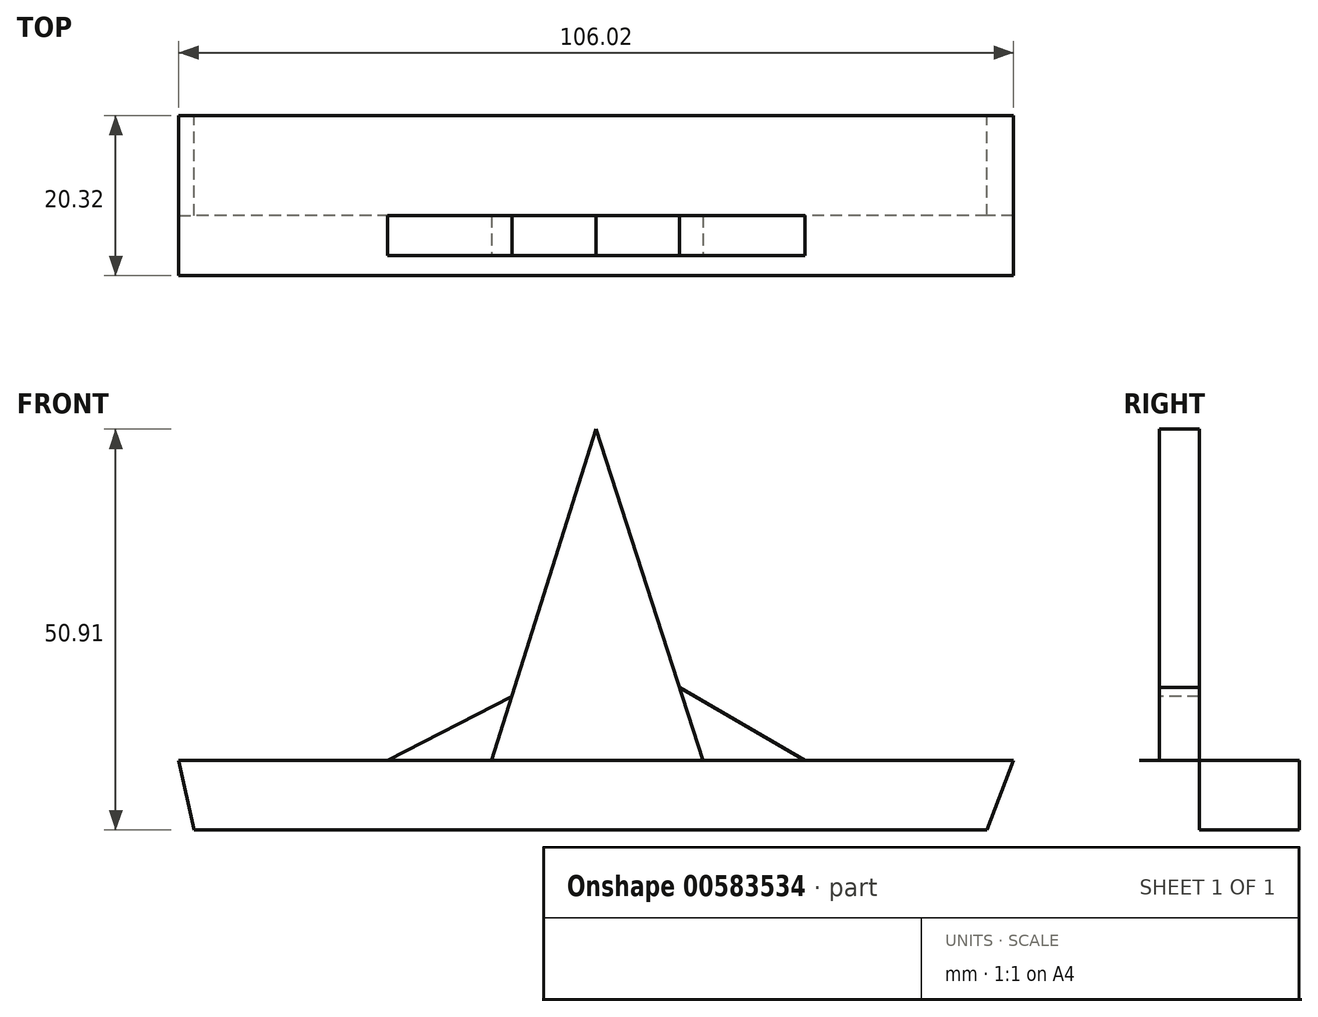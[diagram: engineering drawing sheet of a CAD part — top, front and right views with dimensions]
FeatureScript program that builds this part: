
annotation { "Feature Type Name" : "Feature", "Feature Type Description" : "" }
export const myFeature = defineFeature(function(context is Context, id is Id, definition is map)
    precondition{}
    {
        {
            var Q0;
            Q0=qCreatedBy(makeId("Front.planeOp"),FACE);
            var sketch = newSketch(context, id + "F0", { "sketchPlane" : qUnion([Q0])});
            skLineSegment(sketch, "E0", {"start": v(0, 0) * mm, "end": v(53.01, 0) * mm, "construction": true});
            skLineSegment(sketch, "E1", {"start": v(0, 0) * mm, "end": v(-53.01, 0) * mm, "construction": true});
            skLineSegment(sketch, "E2", {"start": v(-13.29, 0) * mm, "end": v(0, 42.1) * mm});
            skLineSegment(sketch, "E3", {"start": v(0, 42.1) * mm, "end": v(13.57, 0) * mm});
            skLineSegment(sketch, "E4", {"start": v(-53.01, 0) * mm, "end": v(-51.06, -8.81) * mm});
            skLineSegment(sketch, "E5", {"start": v(53.01, 0) * mm, "end": v(49.66, -8.81) * mm});
            skLineSegment(sketch, "E6", {"start": v(49.66, -8.81) * mm, "end": v(-51.06, -8.81) * mm});
            skLineSegment(sketch, "E7", {"start": v(-26.5, 0) * mm, "end": v(-10.71, 8.16) * mm});
            skLineSegment(sketch, "E8", {"start": v(26.5, 0) * mm, "end": v(10.57, 9.3) * mm});
            skLineSegment(sketch, "E9", {"start": v(-53.01, 0) * mm, "end": v(53.01, 0) * mm});
            skSolve(sketch);
        }
        {
            var Q0;
            Q0=sQuery(id+"F0.wireOp",EDGE,"E2");
            var Q1;
            Q1=sQuery(id+"F0.wireOp",EDGE,"E3");
            extrude(context, id + "F1", {"bodyType" : ToolBodyType.SURFACE, "surfaceEntities" : qUnion([Q0, Q1]), "depth" : 5.08 * mm, "offsetDistance" : 25.4 * mm});
        }
        {
            var Q0;
            Q0=sQuery(id+"F0.wireOp",EDGE,"E8");
            var Q1;
            Q1=sQuery(id+"F0.wireOp",EDGE,"E7");
            extrude(context, id + "F2", {"bodyType" : ToolBodyType.SURFACE, "surfaceEntities" : qUnion([Q0, Q1]), "depth" : 5.08 * mm, "offsetDistance" : 25.4 * mm});
        }
        {
            var Q0;
            Q0=sQuery(id+"F0.wireOp",EDGE,"E6");
            var Q1;
            Q1=sQuery(id+"F0.wireOp",EDGE,"E4");
            var Q2;
            Q2=sQuery(id+"F0.wireOp",EDGE,"E5");
            extrude(context, id + "F3", {"bodyType" : ToolBodyType.SURFACE, "surfaceEntities" : qUnion([Q0, Q1, Q2]), "oppositeDirection" : true, "depth" : 12.7 * mm, "offsetDistance" : 25.4 * mm});
        }
        {
            var Q0;
            Q0=sQuery(id+"F0.wireOp",EDGE,"E9");
            extrude(context, id + "F4", {"bodyType" : ToolBodyType.SURFACE, "surfaceEntities" : qUnion([Q0]), "depth" : 7.62 * mm, "offsetDistance" : 25.4 * mm, "hasSecondDirection" : true, "secondDirectionOppositeDirection" : true, "secondDirectionDepth" : 12.7 * mm});
        }
    });
